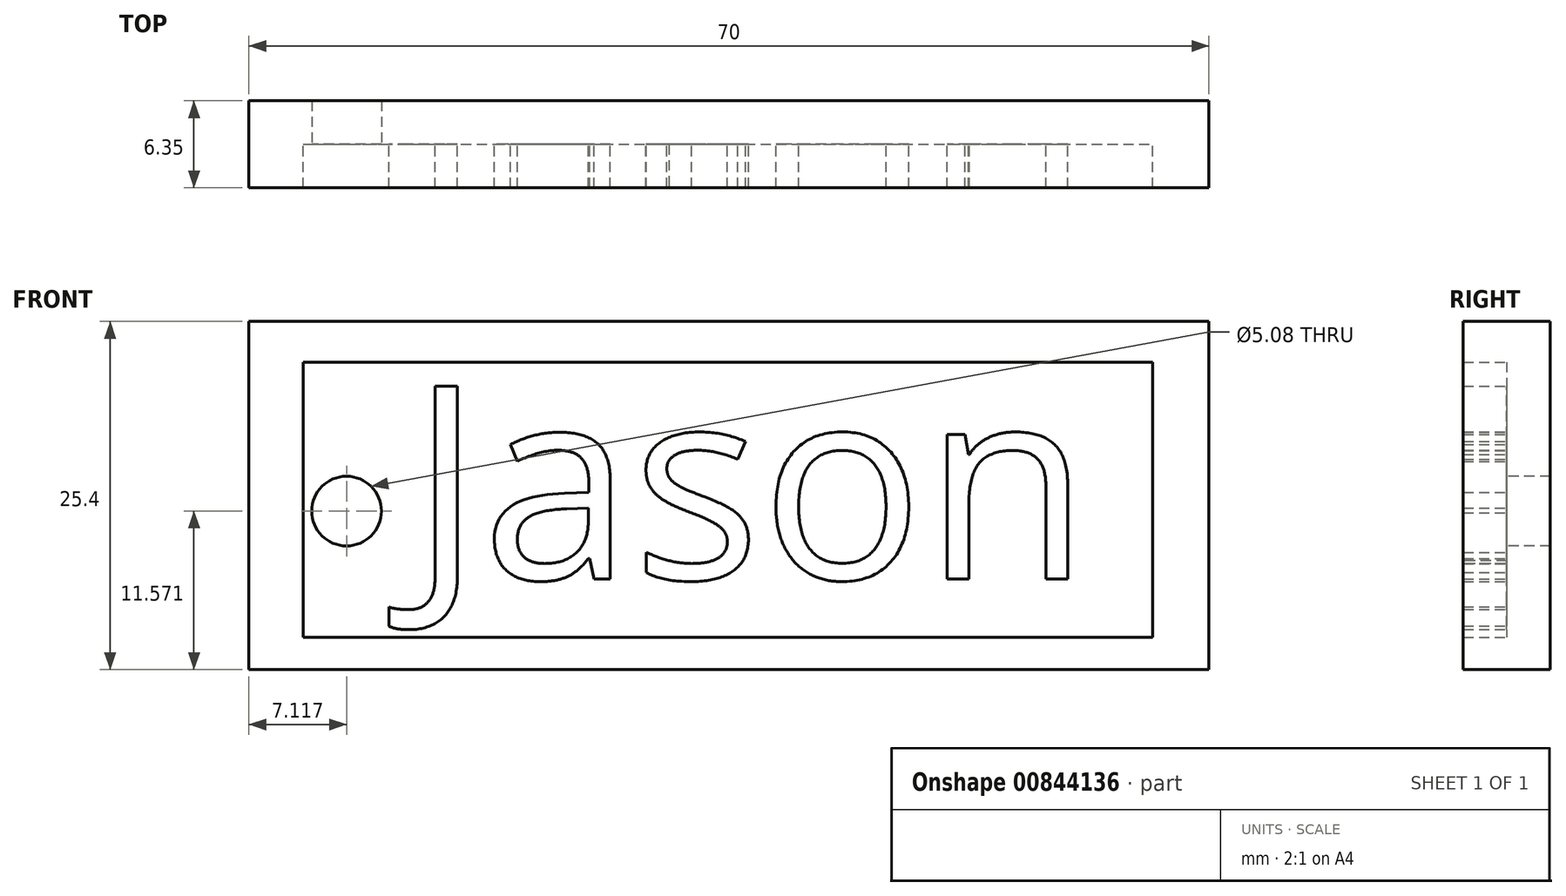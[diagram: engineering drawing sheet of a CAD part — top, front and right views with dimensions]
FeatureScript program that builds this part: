
annotation { "Feature Type Name" : "Feature", "Feature Type Description" : "" }
export const myFeature = defineFeature(function(context is Context, id is Id, definition is map)
    precondition{}
    {
        {
            var Q0;
            Q0=qCreatedBy(makeId("Front.planeOp"),FACE);
            var sketch = newSketch(context, id + "F0", { "sketchPlane" : qUnion([Q0])});
            skLineSegment(sketch, "E0", {"start": v(0, 0) * mm, "end": v(0, 25.4) * mm});
            skLineSegment(sketch, "E1", {"start": v(0, 25.4) * mm, "end": v(70, 25.4) * mm});
            skLineSegment(sketch, "E2", {"start": v(70, 25.4) * mm, "end": v(70, 0) * mm});
            skLineSegment(sketch, "E3", {"start": v(70, 0) * mm, "end": v(0, 0) * mm});
            skLineSegment(sketch, "E4.bottom", {"start": v(3.96, 22.44) * mm, "end": v(65.92, 22.44) * mm});
            skLineSegment(sketch, "E4.top", {"start": v(3.96, 2.35) * mm, "end": v(65.92, 2.35) * mm});
            skLineSegment(sketch, "E4.left", {"start": v(3.96, 22.44) * mm, "end": v(3.96, 2.35) * mm});
            skLineSegment(sketch, "E4.right", {"start": v(65.92, 22.44) * mm, "end": v(65.92, 2.35) * mm});
            skSolve(sketch);
        }
        {
            var Q0;
            Q0 = qSketchRegion(id + "F0", true);
            extrude(context, id + "F1", {"entities" : qUnion([Q0]), "depth" : 6.35 * mm, "offsetDistance" : 25.4 * mm});
        }
        {
            var Q0;
            Q0=makeQuery(id+"F0.imprint","IMPRINT",FACE,{"disambiguationData":[TD([[makeQuery(id+"F0.imprint","IMPRINT",EDGE,{"derivedFrom":sQuery(id+"F0.wireOp",EDGE,"E4.bottom")}),-1.0]])]});
            extrude(context, id + "F2", {"entities" : qUnion([Q0]), "operationType" : NewBodyOperationType.ADD, "depth" : 3.17 * mm, "offsetDistance" : 25.4 * mm});
        }
        {
            var Q0;
            {var subQ0=sQuery(id+"F0.wireOp",EDGE,"E4.bottom");var subQ1=sQuery(id+"F0.wireOp",EDGE,"E4.top");var subQ2=sQuery(id+"F0.wireOp",EDGE,"E4.left");var subQ3=sQuery(id+"F0.wireOp",EDGE,"E4.right");Q0=makeQuery(id+"FwWE98SV1Cmm2kw_1.boolean.opBoolean","SPLIT",FACE,{"disambiguationData":[TD([makeQuery(id+"F1.opExtrude","SWEPT_FACE",FACE,{"disambiguationData":[OSD([subQ0])]})])],"derivedFrom":makeQuery(id+"F2.opExtrude","CAP_FACE",FACE,{"disambiguationData":[OSD([subQ0,subQ1,subQ2,subQ3])],"isStart":false})});}
            var sketch = newSketch(context, id + "F3", { "sketchPlane" : qUnion([Q0])});
            skCircle(sketch, "E5", {"center": v(7.12, 11.57) * mm, "radius": 2.54 * mm});
            skSolve(sketch);
        }
        {
            var Q0;
            Q0 = qSketchRegion(id + "F3", true);
            extrude(context, id + "F4", {"entities" : qUnion([Q0]), "operationType" : NewBodyOperationType.REMOVE, "oppositeDirection" : true, "depth" : 25.4 * mm, "offsetDistance" : 25.4 * mm});
        }
        {
            var Q0;
            Q0=makeQuery(id+"F2.opExtrude","CAP_FACE",FACE,{"disambiguationData":[OSD([sQuery(id+"F0.wireOp",EDGE,"E4.bottom"),sQuery(id+"F0.wireOp",EDGE,"E4.top"),sQuery(id+"F0.wireOp",EDGE,"E4.left"),sQuery(id+"F0.wireOp",EDGE,"E4.right")])],"isStart":false});
            var sketch = newSketch(context, id + "F5", { "sketchPlane" : qUnion([Q0])});
            skText(sketch, "E6", { "text": "Jason", "fontName": "OpenSans-Regular.ttf"});
            const initialGuessF5  = {"E6": [0.01174, 0.00662, 1, 0, 0.01417]};
            skSetInitialGuess(sketch, initialGuessF5);
            skSolve(sketch);
        }
        {
            var Q0;
            Q0 = qSketchRegion(id + "F5", true);
            extrude(context, id + "F6", {"entities" : qUnion([Q0]), "operationType" : NewBodyOperationType.ADD, "depth" : 3.17 * mm, "offsetDistance" : 25.4 * mm});
        }
    });
